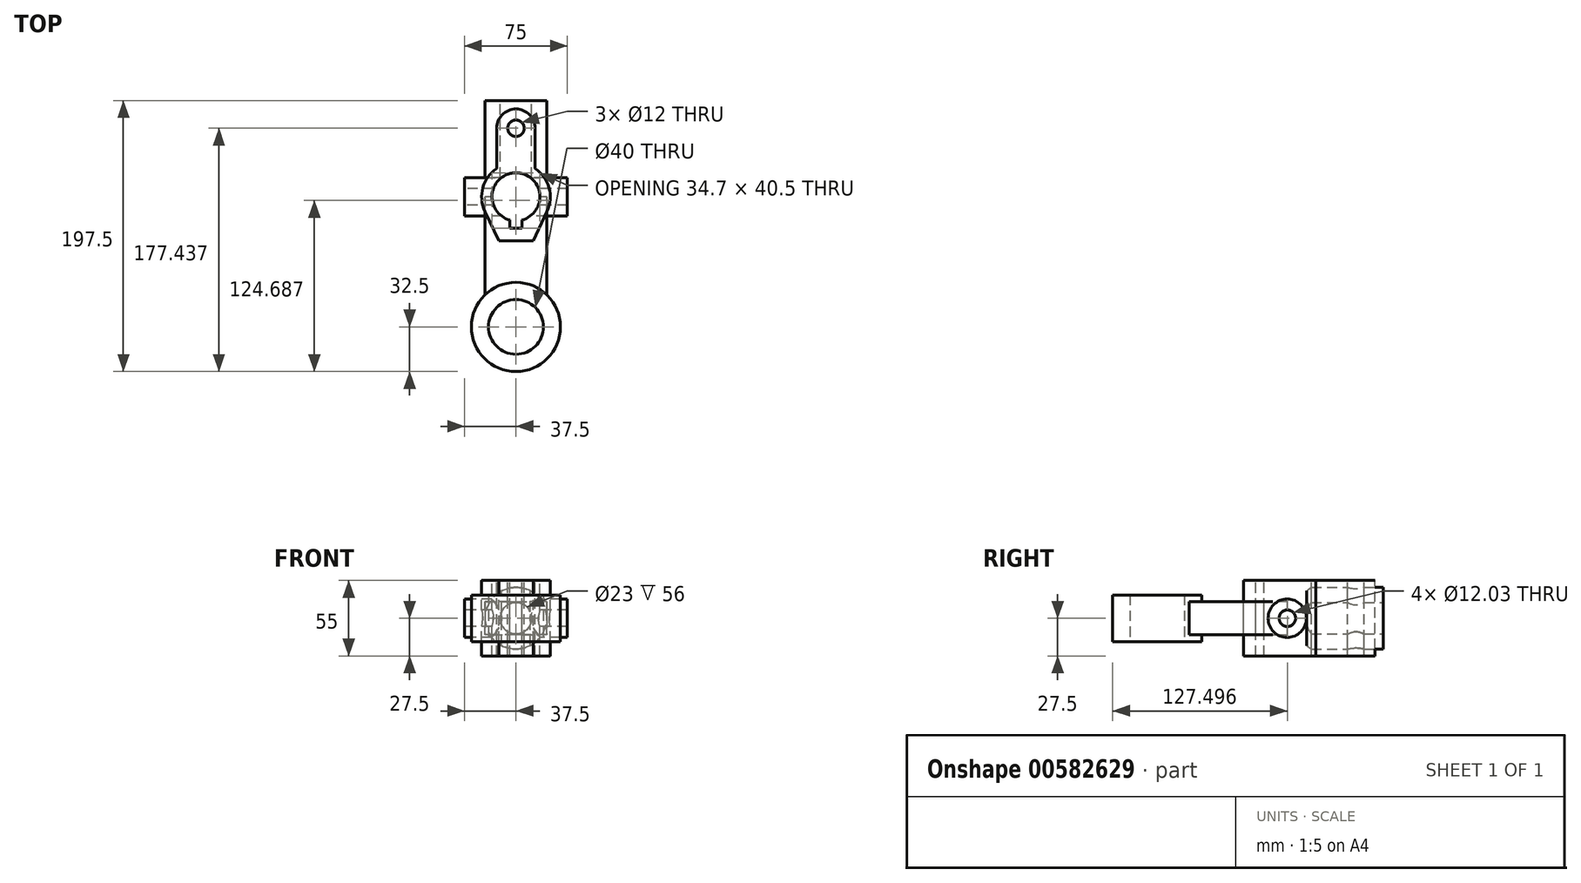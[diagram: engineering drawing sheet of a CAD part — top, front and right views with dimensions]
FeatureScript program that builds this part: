
annotation { "Feature Type Name" : "Feature", "Feature Type Description" : "" }
export const myFeature = defineFeature(function(context is Context, id is Id, definition is map)
    precondition{}
    {
        {
            var Q0;
            Q0=qCreatedBy(makeId("Top.planeOp"),FACE);
            var sketch = newSketch(context, id + "F0", { "sketchPlane" : qUnion([Q0])});
            skCircle(sketch, "E0", {"center": v(0, 0) * mm, "radius": 32.5 * mm});
            skCircle(sketch, "E1", {"center": v(0, 0) * mm, "radius": 20 * mm});
            skSolve(sketch);
        }
        {
            var Q0;
            Q0 = qSketchRegion(id + "F0", true);
            extrude(context, id + "F1", {"entities" : qUnion([Q0]), "endBound" : BoundingType.SYMMETRIC, "depth" : 34 * mm, "offsetDistance" : 25 * mm});
        }
        {
            var Q0;
            Q0=qCreatedBy(makeId("Top.planeOp"),FACE);
            var sketch = newSketch(context, id + "F2", { "sketchPlane" : qUnion([Q0])});
            skLineSegment(sketch, "E2", {"start": v(0, 20) * mm, "end": v(0, 95) * mm});
            skLineSegment(sketch, "E3", {"start": v(20, 0) * mm, "end": v(22.5, 0) * mm});
            skLineSegment(sketch, "E4", {"start": v(-20, 0) * mm, "end": v(-22.5, 0) * mm});
            skLineSegment(sketch, "E5.bottom", {"start": v(22.5, 0) * mm, "end": v(20, 0) * mm});
            skLineSegment(sketch, "E5.top", {"start": v(22.5, 95) * mm, "end": v(-22.5, 95) * mm});
            skLineSegment(sketch, "E5.left", {"start": v(22.5, 0) * mm, "end": v(22.5, 95) * mm});
            skLineSegment(sketch, "E5.right", {"start": v(-22.5, 0) * mm, "end": v(-22.5, 95) * mm});
            skCircle(sketch, "E6", {"center": v(0, 0) * mm, "radius": 20 * mm});
            skSolve(sketch);
        }
        {
            var Q0;
            Q0=qCreatedBy(makeId("Right.planeOp"),FACE);
            var sketch = newSketch(context, id + "F3", { "sketchPlane" : qUnion([Q0])});
            skLineSegment(sketch, "E7", {"start": v(0, 0) * mm, "end": v(0, -12) * mm});
            skLineSegment(sketch, "E8", {"start": v(0, 0) * mm, "end": v(0, 12) * mm});
            skLineSegment(sketch, "E9", {"start": v(95, 12) * mm, "end": v(0, 12) * mm});
            skLineSegment(sketch, "E10", {"start": v(0, -12) * mm, "end": v(95, -12) * mm});
            skLineSegment(sketch, "E11", {"start": v(95, -12) * mm, "end": v(95, 12) * mm});
            skSolve(sketch);
        }
        {
            var Q0;
            Q0 = qSketchRegion(id + "F3", true);
            extrude(context, id + "F4", {"entities" : qUnion([Q0]), "operationType" : NewBodyOperationType.ADD, "endBound" : BoundingType.SYMMETRIC, "depth" : 45 * mm, "offsetDistance" : 25 * mm});
        }
        {
            var Q0;
            {var subQ0=sQuery(id+"F2.wireOp",EDGE,"E6");var subQ1=makeQuery(id+"F2.imprint","INTERSECT",VERTEX,{"derivedFrom":[sQuery(id+"F2.wireOp",EDGE,"E2"),subQ0]});Q0=makeQuery(id+"F2.imprint","IMPRINT",FACE,{"disambiguationData":[TD([[makeQuery(id+"F2.imprint","IMPRINT",EDGE,{"disambiguationData":[TD([[subQ1,1.0]])],"derivedFrom":subQ0}),1.0]])]});}
            var sketch = newSketch(context, id + "F5", { "sketchPlane" : qUnion([Q0])});
            skCircle(sketch, "E12", {"center": v(0, 0) * mm, "radius": 20 * mm});
            skSolve(sketch);
        }
        {
            var Q0;
            Q0 = qSketchRegion(id + "F5", true);
            extrude(context, id + "F6", {"entities" : qUnion([Q0]), "operationType" : NewBodyOperationType.REMOVE, "endBound" : BoundingType.SYMMETRIC, "depth" : 100 * mm, "offsetDistance" : 25 * mm});
        }
        {
            var Q0;
            Q0=makeQuery(id+"F4.opExtrude","CAP_FACE",FACE,{"disambiguationData":[OSD([sQuery(id+"F3.wireOp",EDGE,"E7"),sQuery(id+"F3.wireOp",EDGE,"E8"),sQuery(id+"F3.wireOp",EDGE,"E9"),sQuery(id+"F3.wireOp",EDGE,"E10"),sQuery(id+"F3.wireOp",EDGE,"E11")])],"isStart":true});
            cPlane(context, id + "F7", {"entities" : qUnion([Q0]), "cplaneType" : CPlaneType.OFFSET, "offset" : 15 * mm, "width" : 150 * mm, "height" : 150 * mm});
        }
        {
            var Q0;
            Q0=qCreatedBy(id+"F7.planeOp",FACE);
            var sketch = newSketch(context, id + "F8", { "sketchPlane" : qUnion([Q0])});
            skCircle(sketch, "E13", {"center": v(-94.89, 0) * mm, "radius": 14 * mm});
            skSolve(sketch);
        }
        {
            var Q0;
            Q0 = qSketchRegion(id + "F8", true);
            extrude(context, id + "F9", {"entities" : qUnion([Q0]), "oppositeDirection" : true, "depth" : 75 * mm, "offsetDistance" : 25 * mm});
        }
        {
            var Q0;
            Q0=qCreatedBy(id+"F7.planeOp",FACE);
            var sketch = newSketch(context, id + "F10", { "sketchPlane" : qUnion([Q0])});
            skPoint(sketch, "E14", {"position": v(-95, 0) * mm});
            skCircle(sketch, "E15", {"center": v(-95, 0) * mm, "radius": 6 * mm});
            skSolve(sketch);
        }
        {
            var Q0;
            Q0=makeQuery(id+"F10.imprint","IMPRINT",FACE,{"disambiguationData":[TD([[makeQuery(id+"F10.imprint","IMPRINT",EDGE,{"derivedFrom":sQuery(id+"F10.wireOp",EDGE,"E15")}),1.0]])]});
            extrude(context, id + "F11", {"entities" : qUnion([Q0]), "operationType" : NewBodyOperationType.REMOVE, "endBound" : BoundingType.THROUGH_ALL, "oppositeDirection" : true, "depth" : 25 * mm, "offsetDistance" : 25 * mm});
        }
        {
            var Q0;
            Q0=qCreatedBy(makeId("Front.planeOp"),FACE);
            cPlane(context, id + "F12", {"entities" : qUnion([Q0]), "cplaneType" : CPlaneType.OFFSET, "offset" : 165 * mm, "oppositeDirection" : true, "width" : 150 * mm, "height" : 150 * mm});
        }
        {
            var Q0;
            Q0=qCreatedBy(id+"F12.planeOp",FACE);
            var sketch = newSketch(context, id + "F13", { "sketchPlane" : qUnion([Q0])});
            skCircle(sketch, "E16", {"center": v(0, 0) * mm, "radius": 22.5 * mm});
            skSolve(sketch);
        }
        {
            var Q0;
            Q0 = qSketchRegion(id + "F13", true);
            extrude(context, id + "F14", {"entities" : qUnion([Q0]), "depth" : 56 * mm, "offsetDistance" : 25 * mm});
        }
        {
            var Q0;
            Q0=qCreatedBy(id+"F12.planeOp",FACE);
            var sketch = newSketch(context, id + "F15", { "sketchPlane" : qUnion([Q0])});
            skCircle(sketch, "E17", {"center": v(0, 0) * mm, "radius": 11.5 * mm});
            skSolve(sketch);
        }
        {
            var Q0;
            Q0=makeQuery(id+"F15.imprint","IMPRINT",FACE,{"disambiguationData":[TD([[makeQuery(id+"F15.imprint","IMPRINT",EDGE,{"derivedFrom":sQuery(id+"F15.wireOp",EDGE,"E17")}),1.0]])]});
            extrude(context, id + "F16", {"entities" : qUnion([Q0]), "operationType" : NewBodyOperationType.REMOVE, "depth" : 56 * mm, "offsetDistance" : 25 * mm});
        }
        {
            var Q0;
            Q0=qCreatedBy(makeId("Top.planeOp"),FACE);
            cPlane(context, id + "F17", {"entities" : qUnion([Q0]), "cplaneType" : CPlaneType.OFFSET, "offset" : 27.5 * mm, "width" : 150 * mm, "height" : 150 * mm});
        }
        {
            var Q0;
            Q0=qCreatedBy(id+"F17.planeOp",FACE);
            var sketch = newSketch(context, id + "F18", { "sketchPlane" : qUnion([Q0])});
            skArc(sketch, "E18", {"start": v(22.6, 84.23) * mm, "mid": v(24.11, 101.53) * mm, "end": v(14, 115.65) * mm});
            skLineSegment(sketch, "E19", {"start": v(0, 62.94) * mm, "end": v(12.5, 62.94) * mm});
            skLineSegment(sketch, "E20", {"start": v(0, 62.94) * mm, "end": v(-12.5, 62.94) * mm});
            skLineSegment(sketch, "E21", {"start": v(12.5, 62.94) * mm, "end": v(22.6, 84.23) * mm});
            skLineSegment(sketch, "E22", {"start": v(-12.5, 62.94) * mm, "end": v(-22.6, 84.23) * mm});
            skArc(sketch, "E23", {"start": v(14, 144.94) * mm, "mid": v(0, 158.94) * mm, "end": v(-14, 144.94) * mm});
            skLineSegment(sketch, "E24", {"start": v(14, 144.94) * mm, "end": v(14, 115.65) * mm});
            skLineSegment(sketch, "E25", {"start": v(-14, 144.94) * mm, "end": v(-14, 115.65) * mm});
            skArc(sketch, "E26.trimOffspring", {"start": v(-14, 115.65) * mm, "mid": v(-24.11, 101.53) * mm, "end": v(-22.6, 84.23) * mm});
            skSolve(sketch);
        }
        {
            var Q0;
            Q0 = qSketchRegion(id + "F18", true);
            extrude(context, id + "F19", {"entities" : qUnion([Q0]), "oppositeDirection" : true, "depth" : 55 * mm, "offsetDistance" : 25 * mm});
        }
        {
            var Q0;
            Q0=makeQuery(id+"F19.opExtrude","CAP_FACE",FACE,{"disambiguationData":[OSD([sQuery(id+"F18.wireOp",EDGE,"E18"),sQuery(id+"F18.wireOp",EDGE,"E19"),sQuery(id+"F18.wireOp",EDGE,"E20"),sQuery(id+"F18.wireOp",EDGE,"E21"),sQuery(id+"F18.wireOp",EDGE,"E22"),sQuery(id+"F18.wireOp",EDGE,"E23"),sQuery(id+"F18.wireOp",EDGE,"E24"),sQuery(id+"F18.wireOp",EDGE,"E25"),sQuery(id+"F18.wireOp",EDGE,"E26.trimOffspring")])],"isStart":true});
            var sketch = newSketch(context, id + "F20", { "sketchPlane" : qUnion([Q0])});
            skCircle(sketch, "E27", {"center": v(0, 144.94) * mm, "radius": 6 * mm});
            skPoint(sketch, "E28.start.orphan", {"position": v(0, 94.94) * mm});
            skArc(sketch, "E29", {"start": v(4.5, 78.03) * mm, "mid": v(0, 112.44) * mm, "end": v(-4.5, 78.03) * mm});
            skLineSegment(sketch, "E30", {"start": v(0, 71.94) * mm, "end": v(4.5, 71.94) * mm});
            skLineSegment(sketch, "E31", {"start": v(0, 71.94) * mm, "end": v(-4.5, 71.94) * mm});
            skLineSegment(sketch, "E32", {"start": v(-4.5, 71.94) * mm, "end": v(-4.5, 78.03) * mm});
            skLineSegment(sketch, "E33", {"start": v(4.5, 78.03) * mm, "end": v(4.5, 71.94) * mm});
            skSolve(sketch);
        }
        {
            var Q0;
            Q0 = qSketchRegion(id + "F20", true);
            extrude(context, id + "F21", {"entities" : qUnion([Q0]), "operationType" : NewBodyOperationType.REMOVE, "endBound" : BoundingType.THROUGH_ALL, "oppositeDirection" : true, "depth" : 25 * mm, "offsetDistance" : 25 * mm});
        }
        {
            var Q0;
            Q0=qCreatedBy(id+"F7.planeOp",FACE);
            var sketch = newSketch(context, id + "F22", { "sketchPlane" : qUnion([Q0])});
            skCircle(sketch, "E34", {"center": v(-95, 0) * mm, "radius": 6.01 * mm});
            skSolve(sketch);
        }
        {
            var Q0;
            Q0 = qSketchRegion(id + "F22", true);
            extrude(context, id + "F23", {"entities" : qUnion([Q0]), "operationType" : NewBodyOperationType.REMOVE, "endBound" : BoundingType.THROUGH_ALL, "oppositeDirection" : true, "depth" : 25 * mm, "offsetDistance" : 25 * mm});
        }
    });
